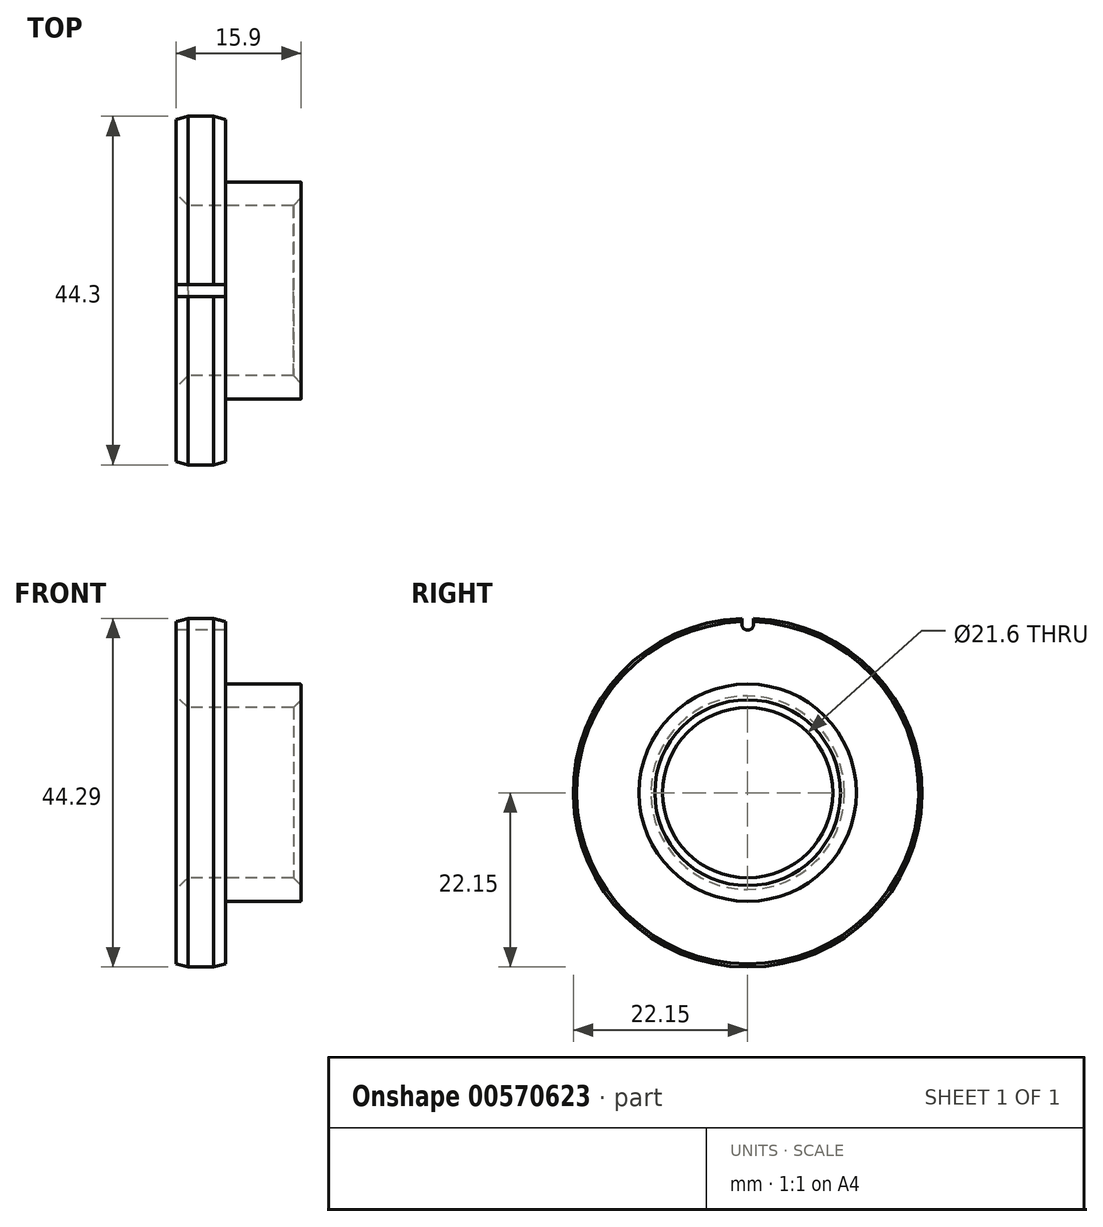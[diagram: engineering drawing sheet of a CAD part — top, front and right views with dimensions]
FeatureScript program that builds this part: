
annotation { "Feature Type Name" : "Feature", "Feature Type Description" : "" }
export const myFeature = defineFeature(function(context is Context, id is Id, definition is map)
    precondition{}
    {
        {
            var Q0;
            Q0=qCreatedBy(makeId("Top.planeOp"),FACE);
            var sketch = newSketch(context, id + "F0", { "sketchPlane" : qUnion([Q0])});
            skLineSegment(sketch, "E0", {"start": v(-15.4, 0) * mm, "end": v(15.14, 0) * mm, "construction": true});
            skLineSegment(sketch, "E1", {"start": v(-21.83, 21.73) * mm, "end": v(-21.83, 10.8) * mm});
            skLineSegment(sketch, "E2", {"start": v(-21.83, 10.8) * mm, "end": v(-5.93, 10.8) * mm});
            skLineSegment(sketch, "E3", {"start": v(-5.93, 10.8) * mm, "end": v(-5.93, 13.8) * mm});
            skLineSegment(sketch, "E4", {"start": v(-5.93, 13.8) * mm, "end": v(-15.53, 13.8) * mm});
            skLineSegment(sketch, "E5", {"start": v(-15.53, 13.8) * mm, "end": v(-15.53, 21.73) * mm});
            skLineSegment(sketch, "E6", {"start": v(-21.83, 21.73) * mm, "end": v(-20.28, 22.15) * mm});
            skLineSegment(sketch, "E7", {"start": v(-15.53, 21.73) * mm, "end": v(-17.08, 22.15) * mm});
            skLineSegment(sketch, "E8", {"start": v(-17.08, 22.15) * mm, "end": v(-20.28, 22.15) * mm});
            skSolve(sketch);
        }
        {
            var Q0;
            Q0=makeQuery(id+"F0.imprint","IMPRINT",FACE,{"disambiguationData":[TD([[makeQuery(id+"F0.imprint","IMPRINT",EDGE,{"derivedFrom":sQuery(id+"F0.wireOp",EDGE,"E1")}),1.0]])]});
            var Q1;
            Q1=sQuery(id+"F0.wireOp",EDGE,"E0");
            revolve(context, id + "F1", {"entities" : qUnion([Q0]), "axis" : qUnion([Q1]), "revolveType" : RevolveType.FULL});
        }
        {
            var Q0;
            Q0=makeQuery(id+"F1.opRevolve","SWEPT_EDGE",EDGE,{"disambiguationData":[OSD([sQuery(id+"F0.wireOp",EDGE,"E2"),sQuery(id+"F0.wireOp",EDGE,"E3")])]});
            chamfer(context, id + "F2", {"entities" : qUnion([Q0]), "width" : 1 * mm, "tangentPropagation" : true});
        }
        {
            var Q0;
            Q0=makeQuery(id+"F1.opRevolve","SWEPT_EDGE",EDGE,{"disambiguationData":[OSD([sQuery(id+"F0.wireOp",EDGE,"E1"),sQuery(id+"F0.wireOp",EDGE,"E2")])]});
            chamfer(context, id + "F3", {"entities" : qUnion([Q0]), "width" : 1.5 * mm, "tangentPropagation" : true});
        }
        {
            var Q0;
            Q0=makeQuery(id+"F1.opRevolve","SWEPT_FACE",FACE,{"disambiguationData":[OSD([sQuery(id+"F0.wireOp",EDGE,"E1")])]});
            var sketch = newSketch(context, id + "F4", { "sketchPlane" : qUnion([Q0])});
            skLineSegment(sketch, "E9", {"start": v(0, -21.73) * mm, "end": v(0, 27.26) * mm});
            skArc(sketch, "E10", {"start": v(-0.75, 21.4) * mm, "mid": v(0, 20.65) * mm, "end": v(0.75, 21.4) * mm});
            skLineSegment(sketch, "E11", {"start": v(0.75, 23.06) * mm, "end": v(0.75, 21.4) * mm});
            skLineSegment(sketch, "E12.MirrorCS", {"start": v(-0.75, 23.06) * mm, "end": v(-0.75, 21.4) * mm});
            skLineSegment(sketch, "E13", {"start": v(-0.75, 23.06) * mm, "end": v(0.75, 23.06) * mm});
            skSolve(sketch);
        }
        {
            var Q0;
            Q0 = qSketchRegion(id + "F4", true);
            var Q1;
            {var subQ0=sQuery(id+"F4.wireOp",EDGE,"E13");var subQ5=sQuery(id+"F4.wireOp",EDGE,"E11");var subQ6=makeQuery(id+"F4.imprint","INTERSECT",VERTEX,{"derivedFrom":[subQ5,subQ0]});Q1=makeQuery(id+"F4.imprint","IMPRINT",FACE,{"disambiguationData":[TD([[makeQuery(id+"F4.imprint","IMPRINT",EDGE,{"disambiguationData":[TD([[subQ6,1.0]])],"derivedFrom":subQ0}),-1.0]])]});}
            var Q2;
            {var subQ0=sQuery(id+"F4.wireOp",EDGE,"E13");var subQ5=sQuery(id+"F4.wireOp",EDGE,"E12.MirrorCS");var subQ6=makeQuery(id+"F4.imprint","INTERSECT",VERTEX,{"derivedFrom":[subQ5,subQ0]});Q2=makeQuery(id+"F4.imprint","IMPRINT",FACE,{"disambiguationData":[TD([[makeQuery(id+"F4.imprint","IMPRINT",EDGE,{"disambiguationData":[TD([[subQ6,-1.0]])],"derivedFrom":subQ0}),-1.0]])]});}
            var Q3;
            {var subQ0=sQuery(id+"F4.wireOp",EDGE,"E10");var subQ5=sQuery(id+"F4.wireOp",EDGE,"E12.MirrorCS");var subQ6=makeQuery(id+"F4.imprint","INTERSECT",VERTEX,{"derivedFrom":[subQ0,subQ5]});Q3=makeQuery(id+"F4.imprint","IMPRINT",FACE,{"disambiguationData":[TD([[makeQuery(id+"F4.imprint","IMPRINT",EDGE,{"disambiguationData":[TD([[subQ6,-1.0]])],"derivedFrom":subQ0}),1.0]])]});}
            var Q4;
            {var subQ0=sQuery(id+"F4.wireOp",EDGE,"E10");var subQ5=sQuery(id+"F4.wireOp",EDGE,"E11");var subQ6=makeQuery(id+"F4.imprint","INTERSECT",VERTEX,{"derivedFrom":[subQ0,subQ5]});Q4=makeQuery(id+"F4.imprint","IMPRINT",FACE,{"disambiguationData":[TD([[makeQuery(id+"F4.imprint","IMPRINT",EDGE,{"disambiguationData":[TD([[subQ6,1.0]])],"derivedFrom":subQ0}),1.0]])]});}
            extrude(context, id + "F5", {"entities" : qUnion([Q0, Q1, Q2, Q3, Q4]), "operationType" : NewBodyOperationType.REMOVE, "oppositeDirection" : true, "depth" : 25 * mm, "offsetDistance" : 25 * mm});
        }
        {
            var Q0;
            Q0=makeQuery(id+"F1.opRevolve","SWEPT_EDGE",EDGE,{"disambiguationData":[OSD([sQuery(id+"F0.wireOp",EDGE,"E4"),sQuery(id+"F0.wireOp",EDGE,"E5")])]});
            var Q1;
            Q1=makeQuery(id+"F1.opRevolve","SWEPT_EDGE",EDGE,{"disambiguationData":[OSD([sQuery(id+"F0.wireOp",EDGE,"E3"),sQuery(id+"F0.wireOp",EDGE,"E4")])]});
            fillet(context, id + "F6", {"entities" : qUnion([Q0, Q1]), "radius" : 0.12 * mm, "tangentPropagation" : true, "allowEdgeOverflow" : false});
        }
    });
